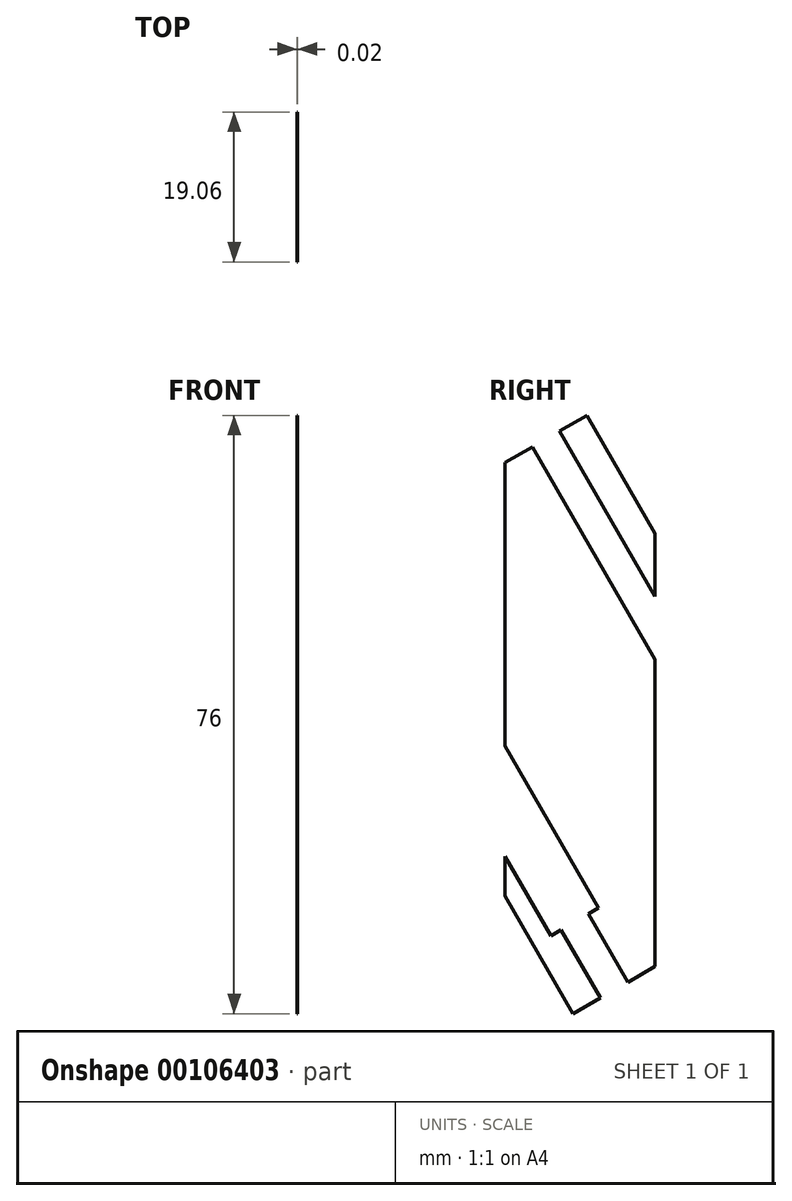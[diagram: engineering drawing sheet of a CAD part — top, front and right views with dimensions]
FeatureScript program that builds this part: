
annotation { "Feature Type Name" : "Feature", "Feature Type Description" : "" }
export const myFeature = defineFeature(function(context is Context, id is Id, definition is map)
    precondition{}
    {
        {
            var Q0;
            Q0=qCreatedBy(makeId("Right.planeOp"),FACE);
            var sketch = newSketch(context, id + "F0", { "sketchPlane" : qUnion([Q0])});
            skLineSegment(sketch, "E0.bottom", {"start": v(-9.52, 69.5) * mm, "end": v(9.53, 80.5) * mm});
            skLineSegment(sketch, "E0.top", {"start": v(-9.52, -5.5) * mm, "end": v(9.53, 5.5) * mm});
            skLineSegment(sketch, "E0.left", {"start": v(-9.52, 69.5) * mm, "end": v(-9.52, -5.5) * mm});
            skLineSegment(sketch, "E0.right", {"start": v(9.53, 80.5) * mm, "end": v(9.53, 5.5) * mm});
            skLineSegment(sketch, "E1", {"start": v(-0.87, -0.5) * mm, "end": v(-9.52, 14.5) * mm});
            skLineSegment(sketch, "E2", {"start": v(0.87, 75.5) * mm, "end": v(9.53, 60.5) * mm});
            skSolve(sketch);
        }
        {
            var Q0;
            {var subQ7=sQuery(id+"F0.wireOp",EDGE,"E1");Q0=makeQuery(id+"F0.imprint","IMPRINT",FACE,{"disambiguationData":[TD([[makeQuery(id+"F0.imprint","IMPRINT",EDGE,{"derivedFrom":subQ7}),-1.0]])]});}
            extrude(context, id + "F1", {"entities" : qUnion([Q0]), "depth" : 3 / 203.2 * mm, "symmetric" : true});
        }
        {
            var Q0;
            Q0=makeQuery(id+"F1.opExtrude","SWEPT_FACE",FACE,{"disambiguationData":[OSD([sQuery(id+"F0.wireOp",EDGE,"E0.top")])]});
            var sketch = newSketch(context, id + "F2", { "sketchPlane" : qUnion([Q0])});
            skCircle(sketch, "E3", {"center": v(0, -5) * mm, "radius": 2 * mm});
            skLineSegment(sketch, "E4", {"start": v(4.76, 1) * mm, "end": v(-4.76, -11) * mm, "construction": true});
            skSolve(sketch);
        }
        {
            var Q0;
            Q0=makeQuery(id+"F2.imprint","IMPRINT",FACE,{"disambiguationData":[TD([[makeQuery(id+"F2.imprint","IMPRINT",EDGE,{"derivedFrom":sQuery(id+"F2.wireOp",EDGE,"E3")}),1.0]])]});
            extrude(context, id + "F3", {"entities" : qUnion([Q0]), "operationType" : NewBodyOperationType.ADD, "oppositeDirection" : true, "depth" : 50 * mm});
        }
        {
            var Q0;
            Q0=makeQuery(id+"F3.opExtrude","CAP_FACE",FACE,{"disambiguationData":[OSD([sQuery(id+"F2.wireOp",EDGE,"E3")])],"isStart":false});
            var sketch = newSketch(context, id + "F4", { "sketchPlane" : qUnion([Q0])});
            skCircle(sketch, "E5", {"center": v(0, 5) * mm, "radius": 3.5 * mm});
            skSolve(sketch);
        }
        {
            var Q0;
            Q0=makeQuery(id+"F4.imprint","IMPRINT",FACE,{"disambiguationData":[TD([[makeQuery(id+"F4.imprint","IMPRINT",EDGE,{"derivedFrom":sQuery(id+"F4.wireOp",EDGE,"E5")}),1.0]])]});
            var Q1;
            Q1=makeQuery(id+"F4.imprint","IMPRINT",FACE,{"disambiguationData":[TD([[makeQuery(id+"F4.imprint","IMPRINT",EDGE,{"derivedFrom":makeQuery(id+"F3.opExtrude","CAP_EDGE",EDGE,{"disambiguationData":[OSD([sQuery(id+"F2.wireOp",EDGE,"E3")])],"isStart":false})}),-1.0]])]});
            extrude(context, id + "F5", {"entities" : qUnion([Q0, Q1]), "operationType" : NewBodyOperationType.REMOVE, "oppositeDirection" : true, "depth" : 40 * mm});
        }
        {
            var Q0;
            Q0=makeQuery(id+"F5.boolean.opBoolean","COPY",FACE,{"derivedFrom":makeQuery(id+"F5.opExtrude","CAP_FACE",FACE,{"disambiguationData":[OSD([sQuery(id+"F4.wireOp",EDGE,"E5")])],"isStart":false})});
            var sketch = newSketch(context, id + "F6", { "sketchPlane" : qUnion([Q0])});
            skCircle(sketch, "E6", {"center": v(0, 5) * mm, "radius": 2 * mm});
            skSolve(sketch);
        }
        {
            var Q0;
            Q0=makeQuery(id+"F6.imprint","IMPRINT",FACE,{"disambiguationData":[TD([[makeQuery(id+"F6.imprint","IMPRINT",EDGE,{"derivedFrom":sQuery(id+"F6.wireOp",EDGE,"E6")}),1.0]])]});
            extrude(context, id + "F7", {"entities" : qUnion([Q0]), "operationType" : NewBodyOperationType.REMOVE, "endBound" : BoundingType.THROUGH_ALL, "oppositeDirection" : true, "depth" : 25 * mm});
        }
        {
            var Q0;
            Q0=makeQuery(id+"F1.opExtrude","SWEPT_FACE",FACE,{"disambiguationData":[OSD([sQuery(id+"F0.wireOp",EDGE,"E0.bottom")])]});
            var sketch = newSketch(context, id + "F8", { "sketchPlane" : qUnion([Q0])});
            skLineSegment(sketch, "E7", {"start": v(4.76, 26.5) * mm, "end": v(-4.76, 26.5) * mm, "construction": true});
            skCircle(sketch, "E8", {"center": v(0, 32.5) * mm, "radius": 2 * mm});
            skLineSegment(sketch, "E9", {"start": v(4.76, 38.5) * mm, "end": v(-4.76, 26.5) * mm, "construction": true});
            skSolve(sketch);
        }
        {
            var Q0;
            Q0=makeQuery(id+"F8.imprint","IMPRINT",FACE,{"disambiguationData":[TD([[makeQuery(id+"F8.imprint","IMPRINT",EDGE,{"derivedFrom":sQuery(id+"F8.wireOp",EDGE,"E8")}),1.0]])]});
            extrude(context, id + "F9", {"entities" : qUnion([Q0]), "operationType" : NewBodyOperationType.REMOVE, "endBound" : BoundingType.THROUGH_ALL, "oppositeDirection" : true, "depth" : 25 * mm});
        }
    });
